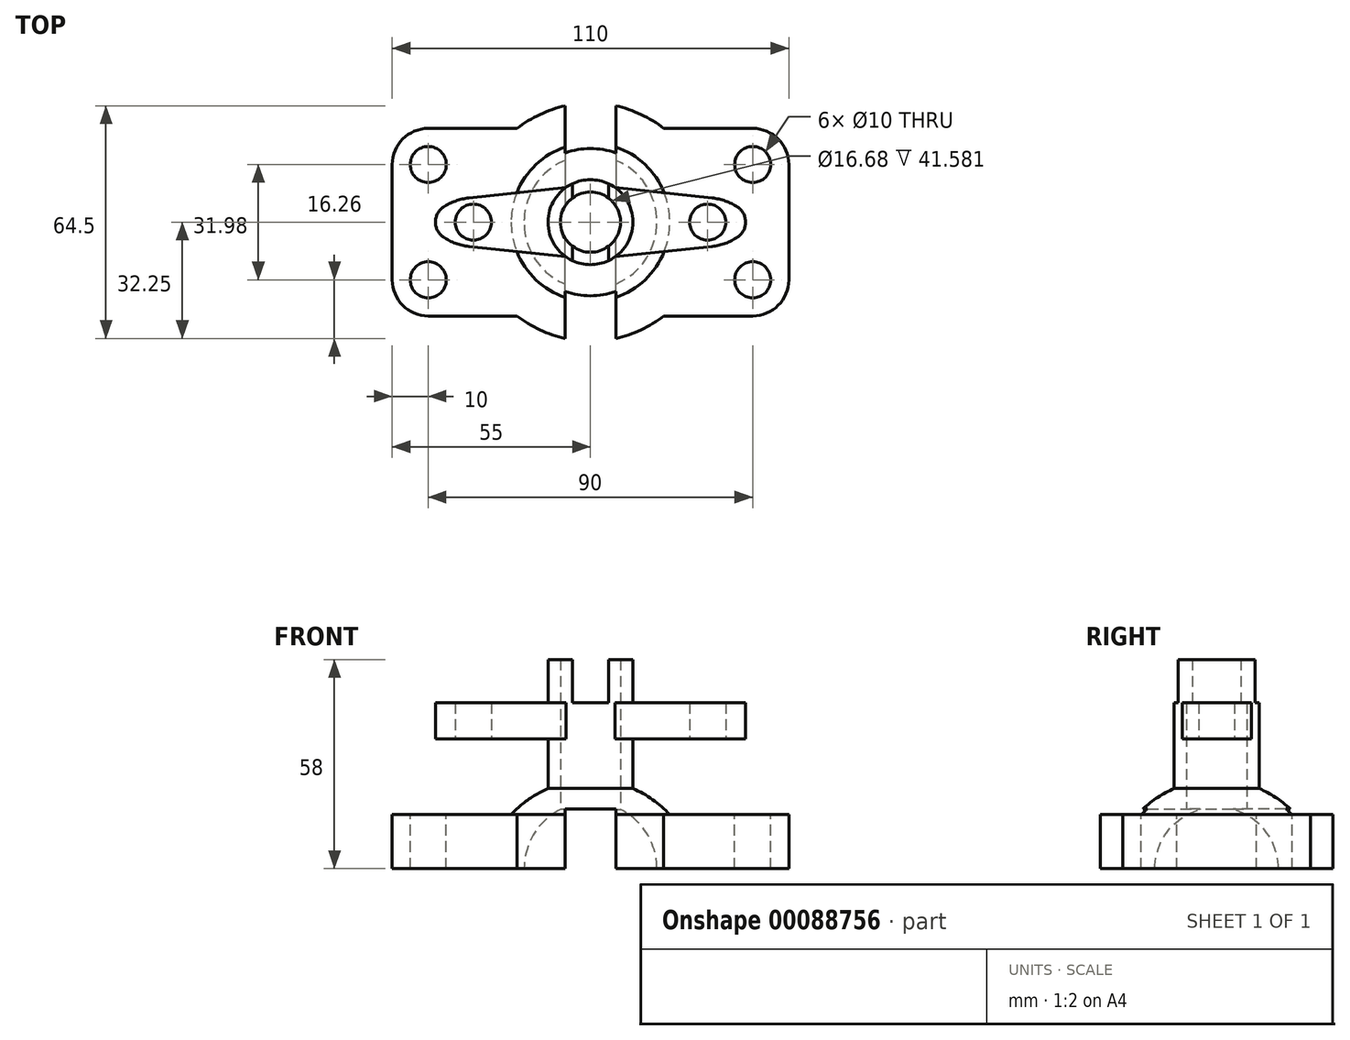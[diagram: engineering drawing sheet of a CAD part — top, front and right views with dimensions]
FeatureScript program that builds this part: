
annotation { "Feature Type Name" : "Feature", "Feature Type Description" : "" }
export const myFeature = defineFeature(function(context is Context, id is Id, definition is map)
    precondition{}
    {
        {
            var Q0;
            Q0=qCreatedBy(makeId("Top.planeOp"),FACE);
            var sketch = newSketch(context, id + "F0", { "sketchPlane" : qUnion([Q0])});
            skSolve(sketch);
        }
        {
            var Q0;
            Q0=qCreatedBy(makeId("Top.planeOp"),FACE);
            var sketch = newSketch(context, id + "F1", { "sketchPlane" : qUnion([Q0])});
            skLineSegment(sketch, "E0", {"start": v(55, 0) * mm, "end": v(-55, 0) * mm});
            skLineSegment(sketch, "E1", {"start": v(-55, 0) * mm, "end": v(-55, -26) * mm});
            skLineSegment(sketch, "E2", {"start": v(-55, -26) * mm, "end": v(55, -26) * mm});
            skLineSegment(sketch, "E3", {"start": v(55, 0) * mm, "end": v(55, -26) * mm});
            skArc(sketch, "E4", {"start": v(-33, 0) * mm, "mid": v(0, -33) * mm, "end": v(33, 0) * mm});
            skSolve(sketch);
        }
        {
            var Q0;
            Q0 = qSketchRegion(id + "F1", true);
            var Q1;
            Q1 = qSketchRegion(id + "F0", true);
            extrude(context, id + "F2", {"entities" : qUnion([Q0, Q1]), "oppositeDirection" : true, "depth" : 15 * mm});
        }
        {
            var Q0;
            Q0=qCreatedBy(makeId("Front.planeOp"),FACE);
            var sketch = newSketch(context, id + "F3", { "sketchPlane" : qUnion([Q0])});
            skArc(sketch, "E5", {"start": v(-22, 0) * mm, "mid": v(-12, 7.1) * mm, "end": v(0, 9.6) * mm});
            skLineSegment(sketch, "E6", {"start": v(0, 9.6) * mm, "end": v(0, 0) * mm});
            skLineSegment(sketch, "E7", {"start": v(0, 0) * mm, "end": v(-22, 0) * mm});
            skSolve(sketch);
        }
        {
            var Q0;
            Q0 = qSketchRegion(id + "F3", true);
            var Q1;
            Q1=sQuery(id+"F3.wireOp",EDGE,"E6");
            revolve(context, id + "F4", {"operationType" : NewBodyOperationType.ADD, "entities" : qUnion([Q0]), "axis" : qUnion([Q1]), "revolveType" : RevolveType.ONE_DIRECTION, "oppositeDirection" : true, "angle" : 3.14 * radian});
        }
        {
            var Q0;
            Q0=qCreatedBy(makeId("Top.planeOp"),FACE);
            var sketch = newSketch(context, id + "F5", { "sketchPlane" : qUnion([Q0])});
            skArc(sketch, "E8", {"start": v(-11.78, 0) * mm, "mid": v(0, -11.78) * mm, "end": v(11.78, 0) * mm});
            skLineSegment(sketch, "E9", {"start": v(11.78, 0) * mm, "end": v(-11.78, 0) * mm});
            skSolve(sketch);
        }
        {
            var Q0;
            Q0 = qSketchRegion(id + "F5", true);
            extrude(context, id + "F6", {"entities" : qUnion([Q0]), "operationType" : NewBodyOperationType.ADD, "depth" : 43 * mm});
        }
        {
            var Q0;
            Q0=qCreatedBy(makeId("Top.planeOp"),FACE);
            var sketch = newSketch(context, id + "F7", { "sketchPlane" : qUnion([Q0])});
            skCircle(sketch, "E10", {"center": v(0, 0) * mm, "radius": 8.34 * mm});
            skSolve(sketch);
        }
        {
            var Q0;
            Q0=qCreatedBy(makeId("Front.planeOp"),FACE);
            var sketch = newSketch(context, id + "F8", { "sketchPlane" : qUnion([Q0])});
            skArc(sketch, "E11", {"start": v(18.42, -15.23) * mm, "mid": v(0.1, 3.41) * mm, "end": v(-18.42, -15.01) * mm});
            skLineSegment(sketch, "E12", {"start": v(18.42, -15.23) * mm, "end": v(-18.42, -15.01) * mm});
            skSolve(sketch);
        }
        {
            var Q0;
            Q0 = qSketchRegion(id + "F8", true);
            var Q1;
            Q1=sQuery(id+"F8.wireOp",EDGE,"E12");
            revolve(context, id + "F9", {"operationType" : NewBodyOperationType.REMOVE, "entities" : qUnion([Q0]), "axis" : qUnion([Q1]), "revolveType" : RevolveType.FULL, "oppositeDirection" : true});
        }
        {
            var Q0;
            Q0=qCreatedBy(makeId("Top.planeOp"),FACE);
            cPlane(context, id + "F10", {"entities" : qUnion([Q0]), "cplaneType" : CPlaneType.OFFSET, "offset" : 21 * mm, "width" : 150 * mm, "height" : 150 * mm});
        }
        {
            var Q0;
            Q0=qCreatedBy(id+"F10.planeOp",FACE);
            var sketch = newSketch(context, id + "F11", { "sketchPlane" : qUnion([Q0])});
            skLineSegment(sketch, "E13", {"start": v(0, 0) * mm, "end": v(45, 0) * mm});
            skLineSegment(sketch, "E14", {"start": v(0, 0) * mm, "end": v(0, -10.31) * mm});
            skLineSegment(sketch, "E15", {"start": v(0, -10.31) * mm, "end": v(0, 0) * mm});
            skLineSegment(sketch, "E16.MirrorCS", {"start": v(0, -10.31) * mm, "end": v(33.72, -6.72) * mm});
            skArc(sketch, "E17", {"start": v(33.72, -6.72) * mm, "mid": v(40.1, -4.6) * mm, "end": v(45, 0) * mm});
            skLineSegment(sketch, "E18.MirrorCS", {"start": v(0, 0) * mm, "end": v(-45, 0) * mm});
            skLineSegment(sketch, "E19.MirrorCS", {"start": v(0, -10.31) * mm, "end": v(-33.72, -6.72) * mm});
            skArc(sketch, "E20.MirrorCS", {"start": v(-33.72, -6.72) * mm, "mid": v(-40.1, -4.6) * mm, "end": v(-45, 0) * mm});
            skSolve(sketch);
        }
        {
            var Q0;
            Q0 = qSketchRegion(id + "F11", true);
            extrude(context, id + "F12", {"entities" : qUnion([Q0]), "operationType" : NewBodyOperationType.ADD, "depth" : 10 * mm});
        }
        {
            var Q0;
            Q0 = qSketchRegion(id + "F7", true);
            extrude(context, id + "F13", {"entities" : qUnion([Q0]), "operationType" : NewBodyOperationType.REMOVE, "depth" : 50 * mm, "hasSecondDirection" : true, "secondDirectionOppositeDirection" : true, "secondDirectionDepth" : 25 * mm});
        }
        {
            var Q0;
            Q0=qCreatedBy(makeId("Front.planeOp"),FACE);
            var sketch = newSketch(context, id + "F14", { "sketchPlane" : qUnion([Q0])});
            skLineSegment(sketch, "E21.bottom", {"start": v(5, 43.01) * mm, "end": v(-5, 43.01) * mm});
            skLineSegment(sketch, "E21.top", {"start": v(5, 31.01) * mm, "end": v(-5, 31.01) * mm});
            skLineSegment(sketch, "E21.left", {"start": v(5, 43.01) * mm, "end": v(5, 31.01) * mm});
            skLineSegment(sketch, "E21.right", {"start": v(-5, 43.01) * mm, "end": v(-5, 31.01) * mm});
            skSolve(sketch);
        }
        {
            var Q0;
            Q0=makeQuery(id+"F14.imprint","IMPRINT",FACE,{"disambiguationData":[TD([[makeQuery(id+"F14.imprint","IMPRINT",EDGE,{"derivedFrom":sQuery(id+"F14.wireOp",EDGE,"E21.bottom")}),1.0]])]});
            extrude(context, id + "F15", {"entities" : qUnion([Q0]), "operationType" : NewBodyOperationType.REMOVE, "depth" : 25 * mm});
        }
        {
            var Q0;
            Q0=qCreatedBy(id+"F10.planeOp",FACE);
            var sketch = newSketch(context, id + "F16", { "sketchPlane" : qUnion([Q0])});
            skCircle(sketch, "E22", {"center": v(-45, -16) * mm, "radius": 5 * mm});
            skCircle(sketch, "E23.MirrorC", {"center": v(45, -16) * mm, "radius": 5 * mm});
            skSolve(sketch);
        }
        {
            var Q0;
            Q0 = qSketchRegion(id + "F16", true);
            extrude(context, id + "F17", {"entities" : qUnion([Q0]), "operationType" : NewBodyOperationType.REMOVE, "oppositeDirection" : true, "depth" : 50 * mm});
        }
        {
            var Q0;
            Q0=makeQuery(id+"F2.opExtrude","SWEPT_EDGE",EDGE,{"disambiguationData":[OSD([sQuery(id+"F1.wireOp",EDGE,"E1"),sQuery(id+"F1.wireOp",EDGE,"E2")])]});
            var Q1;
            Q1=makeQuery(id+"F2.opExtrude","SWEPT_EDGE",EDGE,{"disambiguationData":[OSD([sQuery(id+"F1.wireOp",EDGE,"E2"),sQuery(id+"F1.wireOp",EDGE,"E3")])]});
            fillet(context, id + "F18", {"entities" : qUnion([Q0, Q1]), "radius" : 10 * mm, "tangentPropagation" : true, "allowEdgeOverflow" : false});
        }
        {
            var Q0;
            Q0=qCreatedBy(makeId("Front.planeOp"),FACE);
            var sketch = newSketch(context, id + "F19", { "sketchPlane" : qUnion([Q0])});
            skLineSegment(sketch, "E24.bottom", {"start": v(-7, 1.58) * mm, "end": v(7, 1.58) * mm});
            skLineSegment(sketch, "E24.top", {"start": v(-7, -18.96) * mm, "end": v(7, -18.96) * mm});
            skLineSegment(sketch, "E24.left", {"start": v(-7, 1.58) * mm, "end": v(-7, -18.96) * mm});
            skLineSegment(sketch, "E24.right", {"start": v(7, 1.58) * mm, "end": v(7, -18.96) * mm});
            skSolve(sketch);
        }
        {
            var Q0;
            Q0 = qSketchRegion(id + "F19", true);
            extrude(context, id + "F20", {"entities" : qUnion([Q0]), "operationType" : NewBodyOperationType.REMOVE, "depth" : 70 * mm});
        }
        {
            var Q0;
            Q0=makeQuery(id+"F2.opExtrude","SWEPT_BODY",BODY,{"disambiguationData":[OSD([sQuery(id+"F1.wireOp",EDGE,"E0"),sQuery(id+"F1.wireOp",EDGE,"E1"),sQuery(id+"F1.wireOp",EDGE,"E2"),sQuery(id+"F1.wireOp",EDGE,"E3"),sQuery(id+"F1.wireOp",EDGE,"E4")])]});
            var Q1;
            Q1=qCreatedBy(makeId("Front.planeOp"),FACE);
            mirror(context, id + "F21", {"operationType" : NewBodyOperationType.ADD, "entities" : qUnion([Q0]), "mirrorPlane" : qUnion([Q1])});
        }
        {
            var Q0;
            {var subQ0=makeQuery(id+"F12.opExtrude","SWEPT_EDGE",EDGE,{"disambiguationData":[OSD([sQuery(id+"F11.wireOp",EDGE,"E18.MirrorCS"),sQuery(id+"F11.wireOp",EDGE,"E20.MirrorCS")])]});Q0=makeQuery(id+"F21.boolean.opBoolean","MERGE",EDGE,{"derivedFrom":[subQ0,makeQuery(id+"F21.opPattern","COPY",EDGE,{"derivedFrom":subQ0,"instanceName":"1"})]});}
            fillet(context, id + "F22", {"entities" : qUnion([Q0]), "radius" : 5 * mm, "tangentPropagation" : true, "allowEdgeOverflow" : false});
        }
        {
            var Q0;
            {var subQ0=makeQuery(id+"F12.opExtrude","SWEPT_EDGE",EDGE,{"disambiguationData":[OSD([sQuery(id+"F11.wireOp",EDGE,"E13"),sQuery(id+"F11.wireOp",EDGE,"E17")])]});Q0=makeQuery(id+"F21.boolean.opBoolean","MERGE",EDGE,{"derivedFrom":[subQ0,makeQuery(id+"F21.opPattern","COPY",EDGE,{"derivedFrom":subQ0,"instanceName":"1"})]});}
            fillet(context, id + "F23", {"entities" : qUnion([Q0]), "radius" : 5 * mm, "tangentPropagation" : true, "allowEdgeOverflow" : false});
        }
        {
            var Q0;
            Q0=qCreatedBy(id+"F10.planeOp",FACE);
            var sketch = newSketch(context, id + "F24", { "sketchPlane" : qUnion([Q0])});
            skCircle(sketch, "E25", {"center": v(32.5, 0) * mm, "radius": 5 * mm});
            skCircle(sketch, "E26.MirrorC", {"center": v(-32.5, 0) * mm, "radius": 5 * mm});
            skSolve(sketch);
        }
        {
            var Q0;
            Q0 = qSketchRegion(id + "F24", true);
            extrude(context, id + "F25", {"entities" : qUnion([Q0]), "operationType" : NewBodyOperationType.REMOVE, "depth" : 25 * mm});
        }
    });
